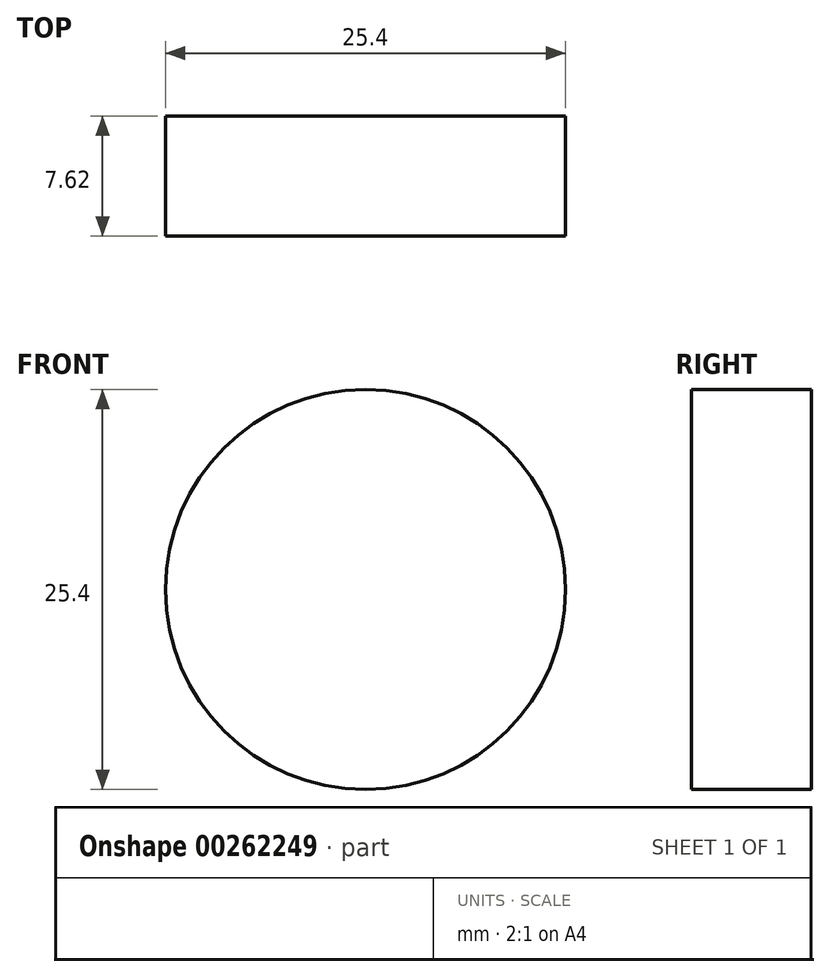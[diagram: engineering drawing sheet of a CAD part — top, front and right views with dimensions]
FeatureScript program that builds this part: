
annotation { "Feature Type Name" : "Feature", "Feature Type Description" : "" }
export const myFeature = defineFeature(function(context is Context, id is Id, definition is map)
    precondition{}
    {
        {
            var Q0;
            Q0=qCreatedBy(makeId("Front.planeOp"),FACE);
            var sketch = newSketch(context, id + "F0", { "sketchPlane" : qUnion([Q0])});
            skCircle(sketch, "E0", {"center": v(0, 0) * mm, "radius": 12.7 * mm});
            skSolve(sketch);
        }
        {
            var Q0;
            Q0=makeQuery(id+"F0.imprint","IMPRINT",FACE,{"disambiguationData":[TD([[makeQuery(id+"F0.imprint","IMPRINT",EDGE,{"derivedFrom":sQuery(id+"F0.wireOp",EDGE,"E0")}),1.0]])]});
            extrude(context, id + "F1", {"entities" : qUnion([Q0]), "depth" : 7.62 * mm});
        }
    });
